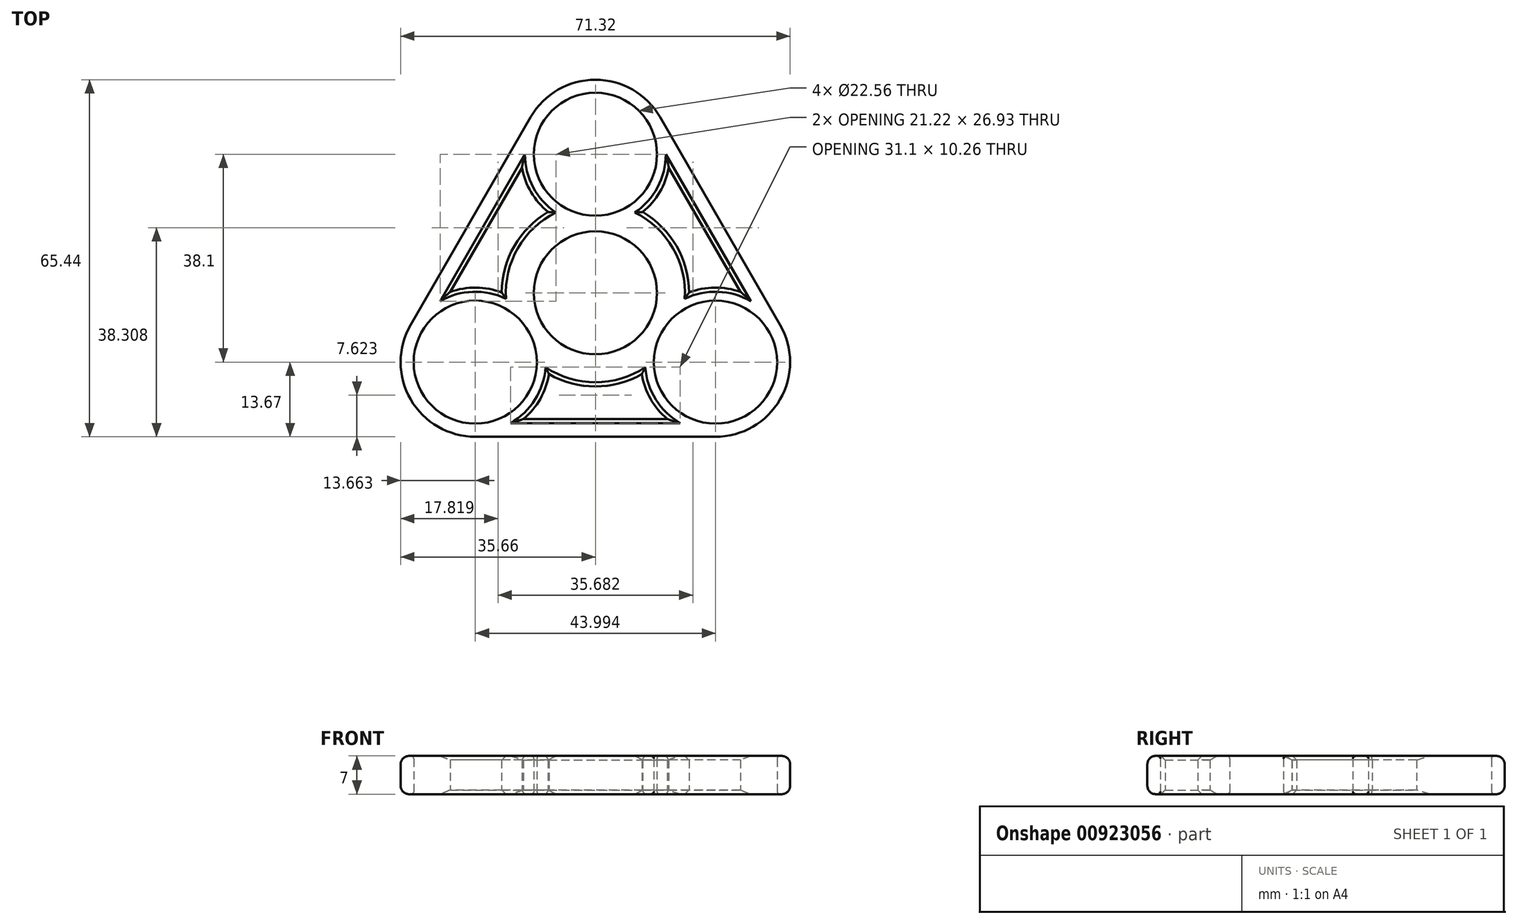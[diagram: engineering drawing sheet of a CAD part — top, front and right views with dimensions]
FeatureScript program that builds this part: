
annotation { "Feature Type Name" : "Feature", "Feature Type Description" : "" }
export const myFeature = defineFeature(function(context is Context, id is Id, definition is map)
    precondition{}
    {
        {
            var Q0;
            Q0=qCreatedBy(makeId("Top.planeOp"),FACE);
            var sketch = newSketch(context, id + "F0", { "sketchPlane" : qUnion([Q0])});
            skCircle(sketch, "E0", {"center": v(0, 0) * mm, "radius": 11.28 * mm});
            skLineSegment(sketch, "E1", {"start": v(0, 0) * mm, "end": v(-51.08, -29.49) * mm});
            skLineSegment(sketch, "E2", {"start": v(0, 0) * mm, "end": v(58.4, -33.72) * mm});
            skCircle(sketch, "E3", {"center": v(0, 25.4) * mm, "radius": 11.28 * mm});
            skCircle(sketch, "E4", {"center": v(22, -12.7) * mm, "radius": 11.28 * mm});
            skCircle(sketch, "E5", {"center": v(-22, -12.7) * mm, "radius": 11.28 * mm});
            skArc(sketch, "E6", {"start": v(11.83, 32.23) * mm, "mid": v(0, 39.07) * mm, "end": v(-11.83, 32.23) * mm});
            skArc(sketch, "E7", {"start": v(-33.83, -5.87) * mm, "mid": v(-33.83, -19.53) * mm, "end": v(-22, -26.37) * mm});
            skArc(sketch, "E8", {"start": v(22, -26.37) * mm, "mid": v(33.83, -19.53) * mm, "end": v(33.83, -5.87) * mm});
            skLineSegment(sketch, "E9", {"start": v(-11.83, 32.23) * mm, "end": v(-33.83, -5.87) * mm});
            skLineSegment(sketch, "E10", {"start": v(11.83, 32.23) * mm, "end": v(33.83, -5.87) * mm});
            skLineSegment(sketch, "E11", {"start": v(22, -26.37) * mm, "end": v(-22, -26.37) * mm});
            skArc(sketch, "E12", {"start": v(-26.6, 0.17) * mm, "mid": v(-21.87, 0.96) * mm, "end": v(-17.16, 0.08) * mm});
            skArc(sketch, "E13", {"start": v(-13.44, 22.94) * mm, "mid": v(-11.77, 18.45) * mm, "end": v(-8.65, 14.82) * mm});
            skLineSegment(sketch, "E14", {"start": v(-13.44, 22.94) * mm, "end": v(-26.6, 0.17) * mm});
            skArc(sketch, "E15", {"start": v(-17.16, 0.08) * mm, "mid": v(-14.86, 8.58) * mm, "end": v(-8.65, 14.82) * mm});
            skArc(sketch, "E16.1.0", {"start": v(8.5, -14.9) * mm, "mid": v(0, -17.16) * mm, "end": v(-8.5, -14.9) * mm});
            skArc(sketch, "E16.1.1", {"start": v(-13.15, -23.11) * mm, "mid": v(-10.1, -19.42) * mm, "end": v(-8.5, -14.9) * mm});
            skLineSegment(sketch, "E16.1.2", {"start": v(-13.15, -23.11) * mm, "end": v(13.15, -23.11) * mm});
            skArc(sketch, "E16.1.3", {"start": v(13.15, -23.11) * mm, "mid": v(10.1, -19.42) * mm, "end": v(8.5, -14.9) * mm});
            skArc(sketch, "E16.2.0", {"start": v(8.65, 14.82) * mm, "mid": v(14.86, 8.58) * mm, "end": v(17.16, 0.08) * mm});
            skArc(sketch, "E16.2.1", {"start": v(26.6, 0.17) * mm, "mid": v(21.87, 0.96) * mm, "end": v(17.16, 0.08) * mm});
            skLineSegment(sketch, "E16.2.2", {"start": v(26.6, 0.17) * mm, "end": v(13.44, 22.94) * mm});
            skArc(sketch, "E16.2.3", {"start": v(13.44, 22.94) * mm, "mid": v(11.77, 18.45) * mm, "end": v(8.65, 14.82) * mm});
            skSolve(sketch);
        }
        {
            var Q0;
            Q0 = qSketchRegion(id + "F0", true);
            extrude(context, id + "F1", {"entities" : qUnion([Q0]), "depth" : 7 * mm, "offsetDistance" : 25.4 * mm});
        }
        {
            var Q0;
            Q0=makeQuery(id+"F1.opExtrude","CAP_EDGE",EDGE,{"disambiguationData":[OSD([sQuery(id+"F0.wireOp",EDGE,"E9")])],"isStart":false});
            var Q1;
            Q1=makeQuery(id+"F1.opExtrude","CAP_EDGE",EDGE,{"disambiguationData":[OSD([sQuery(id+"F0.wireOp",EDGE,"E9")])],"isStart":true});
            fillet(context, id + "F2", {"entities" : qUnion([Q0, Q1]), "radius" : 1.52 * mm, "tangentPropagation" : true, "allowEdgeOverflow" : false});
        }
        {
            var Q0;
            Q0=makeQuery(id+"F1.opExtrude","CAP_EDGE",EDGE,{"disambiguationData":[OSD([sQuery(id+"F0.wireOp",EDGE,"E5")])],"isStart":false});
            var Q1;
            Q1=makeQuery(id+"F1.opExtrude","CAP_EDGE",EDGE,{"disambiguationData":[OSD([sQuery(id+"F0.wireOp",EDGE,"E4")])],"isStart":false});
            var Q2;
            Q2=makeQuery(id+"F1.opExtrude","CAP_EDGE",EDGE,{"disambiguationData":[OSD([sQuery(id+"F0.wireOp",EDGE,"E3")])],"isStart":false});
            var Q3;
            Q3=makeQuery(id+"F1.opExtrude","CAP_EDGE",EDGE,{"disambiguationData":[OSD([sQuery(id+"F0.wireOp",EDGE,"E0")])],"isStart":false});
            var Q4;
            Q4=makeQuery(id+"F1.opExtrude","CAP_EDGE",EDGE,{"disambiguationData":[OSD([sQuery(id+"F0.wireOp",EDGE,"E5")])],"isStart":true});
            var Q5;
            Q5=makeQuery(id+"F1.opExtrude","CAP_EDGE",EDGE,{"disambiguationData":[OSD([sQuery(id+"F0.wireOp",EDGE,"E3")])],"isStart":true});
            var Q6;
            Q6=makeQuery(id+"F1.opExtrude","CAP_EDGE",EDGE,{"disambiguationData":[OSD([sQuery(id+"F0.wireOp",EDGE,"E0")])],"isStart":true});
            var Q7;
            Q7=makeQuery(id+"F1.opExtrude","CAP_EDGE",EDGE,{"disambiguationData":[OSD([sQuery(id+"F0.wireOp",EDGE,"E4")])],"isStart":true});
            fillet(context, id + "F3", {"entities" : qUnion([Q0, Q1, Q2, Q3, Q4, Q5, Q6, Q7]), "radius" : 0.5 * mm, "tangentPropagation" : true, "allowEdgeOverflow" : false});
        }
        {
            var Q0;
            Q0=makeQuery(id+"F1.opExtrude","CAP_EDGE",EDGE,{"disambiguationData":[OSD([sQuery(id+"F0.wireOp",EDGE,"E13")])],"isStart":false});
            var Q1;
            Q1=makeQuery(id+"F1.opExtrude","CAP_EDGE",EDGE,{"disambiguationData":[OSD([sQuery(id+"F0.wireOp",EDGE,"E15")])],"isStart":false});
            var Q2;
            Q2=makeQuery(id+"F1.opExtrude","CAP_EDGE",EDGE,{"disambiguationData":[OSD([sQuery(id+"F0.wireOp",EDGE,"E14")])],"isStart":false});
            var Q3;
            Q3=makeQuery(id+"F1.opExtrude","CAP_EDGE",EDGE,{"disambiguationData":[OSD([sQuery(id+"F0.wireOp",EDGE,"E12")])],"isStart":false});
            var Q4;
            Q4=makeQuery(id+"F1.opExtrude","CAP_EDGE",EDGE,{"disambiguationData":[OSD([sQuery(id+"F0.wireOp",EDGE,"E16.1.1")])],"isStart":true});
            var Q5;
            Q5=makeQuery(id+"F1.opExtrude","CAP_EDGE",EDGE,{"disambiguationData":[OSD([sQuery(id+"F0.wireOp",EDGE,"E16.1.1")])],"isStart":false});
            var Q6;
            Q6=makeQuery(id+"F1.opExtrude","CAP_EDGE",EDGE,{"disambiguationData":[OSD([sQuery(id+"F0.wireOp",EDGE,"E16.1.0")])],"isStart":false});
            var Q7;
            Q7=makeQuery(id+"F1.opExtrude","CAP_EDGE",EDGE,{"disambiguationData":[OSD([sQuery(id+"F0.wireOp",EDGE,"E16.1.3")])],"isStart":false});
            var Q8;
            Q8=makeQuery(id+"F1.opExtrude","CAP_EDGE",EDGE,{"disambiguationData":[OSD([sQuery(id+"F0.wireOp",EDGE,"E16.1.2")])],"isStart":false});
            var Q9;
            Q9=makeQuery(id+"F1.opExtrude","CAP_EDGE",EDGE,{"disambiguationData":[OSD([sQuery(id+"F0.wireOp",EDGE,"E16.2.2")])],"isStart":false});
            var Q10;
            Q10=makeQuery(id+"F1.opExtrude","CAP_EDGE",EDGE,{"disambiguationData":[OSD([sQuery(id+"F0.wireOp",EDGE,"E16.2.0")])],"isStart":false});
            var Q11;
            Q11=makeQuery(id+"F1.opExtrude","CAP_EDGE",EDGE,{"disambiguationData":[OSD([sQuery(id+"F0.wireOp",EDGE,"E16.2.1")])],"isStart":false});
            var Q12;
            Q12=makeQuery(id+"F1.opExtrude","CAP_EDGE",EDGE,{"disambiguationData":[OSD([sQuery(id+"F0.wireOp",EDGE,"E16.2.3")])],"isStart":false});
            var Q13;
            Q13=makeQuery(id+"F1.opExtrude","CAP_EDGE",EDGE,{"disambiguationData":[OSD([sQuery(id+"F0.wireOp",EDGE,"E14")])],"isStart":true});
            var Q14;
            Q14=makeQuery(id+"F1.opExtrude","CAP_EDGE",EDGE,{"disambiguationData":[OSD([sQuery(id+"F0.wireOp",EDGE,"E13")])],"isStart":true});
            var Q15;
            Q15=makeQuery(id+"F1.opExtrude","CAP_EDGE",EDGE,{"disambiguationData":[OSD([sQuery(id+"F0.wireOp",EDGE,"E15")])],"isStart":true});
            var Q16;
            Q16=makeQuery(id+"F1.opExtrude","CAP_EDGE",EDGE,{"disambiguationData":[OSD([sQuery(id+"F0.wireOp",EDGE,"E12")])],"isStart":true});
            var Q17;
            Q17=makeQuery(id+"F1.opExtrude","CAP_EDGE",EDGE,{"disambiguationData":[OSD([sQuery(id+"F0.wireOp",EDGE,"E16.2.3")])],"isStart":true});
            var Q18;
            Q18=makeQuery(id+"F1.opExtrude","CAP_EDGE",EDGE,{"disambiguationData":[OSD([sQuery(id+"F0.wireOp",EDGE,"E16.2.0")])],"isStart":true});
            var Q19;
            Q19=makeQuery(id+"F1.opExtrude","CAP_EDGE",EDGE,{"disambiguationData":[OSD([sQuery(id+"F0.wireOp",EDGE,"E16.2.1")])],"isStart":true});
            var Q20;
            Q20=makeQuery(id+"F1.opExtrude","CAP_EDGE",EDGE,{"disambiguationData":[OSD([sQuery(id+"F0.wireOp",EDGE,"E16.2.2")])],"isStart":true});
            var Q21;
            Q21=makeQuery(id+"F1.opExtrude","CAP_EDGE",EDGE,{"disambiguationData":[OSD([sQuery(id+"F0.wireOp",EDGE,"E16.1.0")])],"isStart":true});
            var Q22;
            Q22=makeQuery(id+"F1.opExtrude","CAP_EDGE",EDGE,{"disambiguationData":[OSD([sQuery(id+"F0.wireOp",EDGE,"E16.1.3")])],"isStart":true});
            var Q23;
            Q23=makeQuery(id+"F1.opExtrude","CAP_EDGE",EDGE,{"disambiguationData":[OSD([sQuery(id+"F0.wireOp",EDGE,"E16.1.2")])],"isStart":true});
            chamfer(context, id + "F4", {"entities" : qUnion([Q0, Q1, Q2, Q3, Q4, Q5, Q6, Q7, Q8, Q9, Q10, Q11, Q12, Q13, Q14, Q15, Q16, Q17, Q18, Q19, Q20, Q21, Q22, Q23]), "width" : 0.76 * mm, "tangentPropagation" : true});
        }
    });
